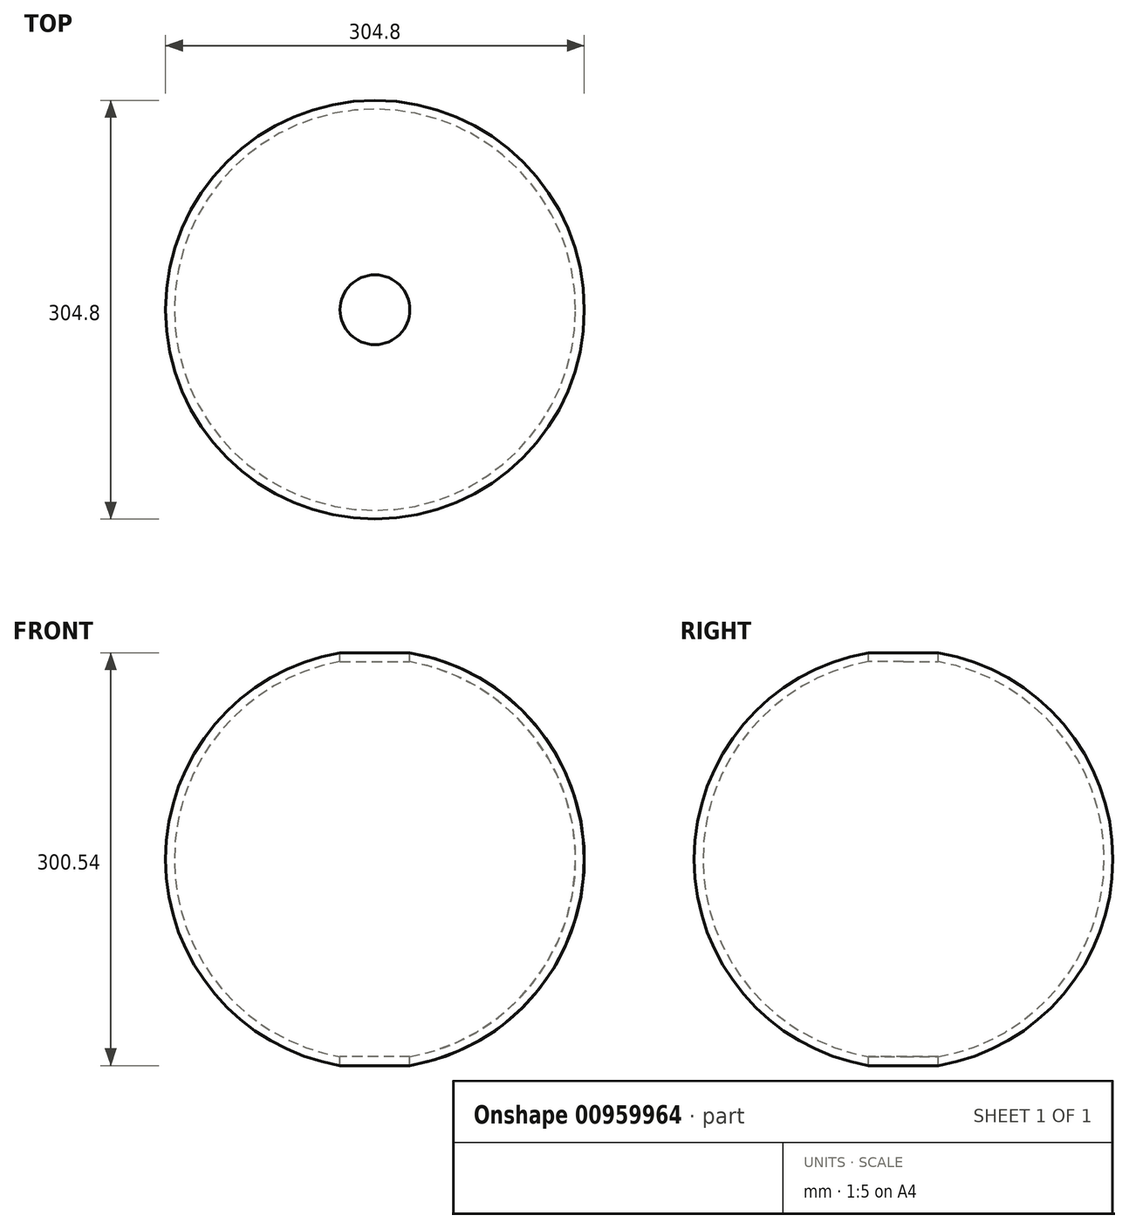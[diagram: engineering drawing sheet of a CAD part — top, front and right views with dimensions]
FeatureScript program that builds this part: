
annotation { "Feature Type Name" : "Feature", "Feature Type Description" : "" }
export const myFeature = defineFeature(function(context is Context, id is Id, definition is map)
    precondition{}
    {
        {
            var Q0;
            Q0=qCreatedBy(makeId("Front.planeOp"),FACE);
            var sketch = newSketch(context, id + "F0", { "sketchPlane" : qUnion([Q0])});
            skCircle(sketch, "E0", {"center": v(0, 0) * mm, "radius": 152.4 * mm});
            skCircle(sketch, "E1.0", {"center": v(0, 0) * mm, "radius": 146.05 * mm});
            skLineSegment(sketch, "E2", {"start": v(0, 152.4) * mm, "end": v(0, -152.4) * mm});
            skSolve(sketch);
        }
        {
            var Q0;
            {var subQ0=sQuery(id+"F0.wireOp",EDGE,"E2");var subQ1=sQuery(id+"F0.wireOp",EDGE,"E0");var subQ2=makeQuery(id+"F0.imprint","INTERSECT",VERTEX,{"disambiguationData":[OD(0.0)],"derivedFrom":[subQ1,subQ0]});Q0=makeQuery(id+"F0.imprint","IMPRINT",FACE,{"disambiguationData":[TD([[makeQuery(id+"F0.imprint","IMPRINT",EDGE,{"disambiguationData":[TD([[subQ2,-1.0]])],"derivedFrom":subQ1}),1.0]])]});}
            var Q1;
            Q1=sQuery(id+"F0.wireOp",EDGE,"E2");
            revolve(context, id + "F1", {"surfaceOperationType" : NewSurfaceOperationType.NEW, "entities" : qUnion([Q0]), "axis" : qUnion([Q1]), "revolveType" : RevolveType.ONE_DIRECTION, "angle" : 180 * degree});
        }
        {
            var Q0;
            Q0=qCreatedBy(makeId("Top.planeOp"),FACE);
            var sketch = newSketch(context, id + "F2", { "sketchPlane" : qUnion([Q0])});
            skCircle(sketch, "E3", {"center": v(0, 0) * mm, "radius": 25.4 * mm});
            skSolve(sketch);
        }
        {
            var Q0;
            Q0=makeQuery(id+"F2.imprint","IMPRINT",FACE,{"disambiguationData":[TD([[makeQuery(id+"F2.imprint","IMPRINT",EDGE,{"derivedFrom":sQuery(id+"F2.wireOp",EDGE,"E3")}),1.0]])]});
            extrude(context, id + "F3", {"entities" : qUnion([Q0]), "operationType" : NewBodyOperationType.REMOVE, "endBound" : BoundingType.SYMMETRIC, "oppositeDirection" : true, "depth" : 304.8 * mm, "offsetDistance" : 25.4 * mm});
        }
        {
            var Q0;
            Q0=makeQuery(id+"F1.opRevolve","SWEPT_BODY",BODY,{"disambiguationData":[OSD([sQuery(id+"F0.wireOp",EDGE,"E0"),sQuery(id+"F0.wireOp",EDGE,"E1.0"),sQuery(id+"F0.wireOp",EDGE,"E2")])]});
            var Q1;
            Q1=qCreatedBy(makeId("Front.planeOp"),FACE);
            mirror(context, id + "F4", {"operationType" : NewBodyOperationType.ADD, "entities" : qUnion([Q0]), "mirrorPlane" : qUnion([Q1])});
        }
    });
